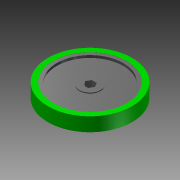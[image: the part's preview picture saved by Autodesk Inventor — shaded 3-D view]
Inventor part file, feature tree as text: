
AUTODESK INVENTOR PART (.ipt)
format: ipt  version: 2012 (Build 160160000, 160)  size: 126,976 bytes
history: native  units: mm
features: extrude x5, sketch x1
ambient origin geometry x8: Origin, YZ Plane, XZ Plane, XY Plane, X Axis, Y Axis, Z Axis, Center Point
bodies: Solid1 (feature_tree)
feature tree (6):
  sketch  "Sketch1"  dims[d0=8.0mm d2=12.7mm d3=12.7mm d4=0.0mm d5=20.32mm d6=0.0mm d7=123.825mm d8=13.0mm d9=10.0mm d10=0.0mm d11=10.0mm d12=0.0mm d13=31.0mm d14=15.24mm d15=0.0mm]
  extrude  "Extrusion1"  Depth=12.7mm
  extrude  "Extrusion2"  Depth=12.7mm TaperAngle=0.0deg
  extrude  "Extrusion3"  Depth=20.32mm TaperAngle=0.0deg
  extrude  "Extrusion4"  Depth=123.825mm
  extrude  "Extrusion5"  Depth=13.0mm
